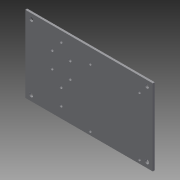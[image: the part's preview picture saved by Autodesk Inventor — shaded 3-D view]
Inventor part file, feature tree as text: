
AUTODESK INVENTOR PART (.ipt)
format: ipt  version: 2014 (Build 180170000, 170)  size: 136,704 bytes
history: native  units: mm
features: extrude x3, sketch x3
ambient origin geometry x8: Origin, YZ Plane, XZ Plane, XY Plane, X Axis, Y Axis, Z Axis, Center Point
bodies: Solid1 (feature_tree)
feature tree (6):
  extrude  "Extrusion1"  Depth=127.0mm
  extrude  "Extrusion2"  Depth=2.0mm
  extrude  "Extrusion3"  Depth=10.0mm
  sketch  "Sketch1"  dims[d0=76.0mm d1=127.0mm]
  sketch  "Sketch2"  dims[d2=2.0mm d3=0.0mm d5=32.6mm]
  sketch  "Sketch3"  dims[d6=57.7mm d7=4.0mm d8=10.0mm d9=0.0mm d10=93.0mm d12=51.0mm d13=10.0mm d14=56.0mm d15=85.0mm d16=27.0mm d17=3.0mm d18=20.0mm d20=55.0mm d21=10.0mm d23=10.0mm d25=0.0mm d27=2.75mm d29=20.0mm d31=58.0mm d32=20.0mm d34=49.0mm d37=10.0mm d38=0.0mm d39=3.5mm d41=3.5mm d42=3.0mm d43=8.98mm d44=27.5mm d45=3.0mm d46=55.0mm d47=3.0mm d48=27.5mm d49=11.0mm d50=8.98mm d51=8.98mm d52=3.0mm]
